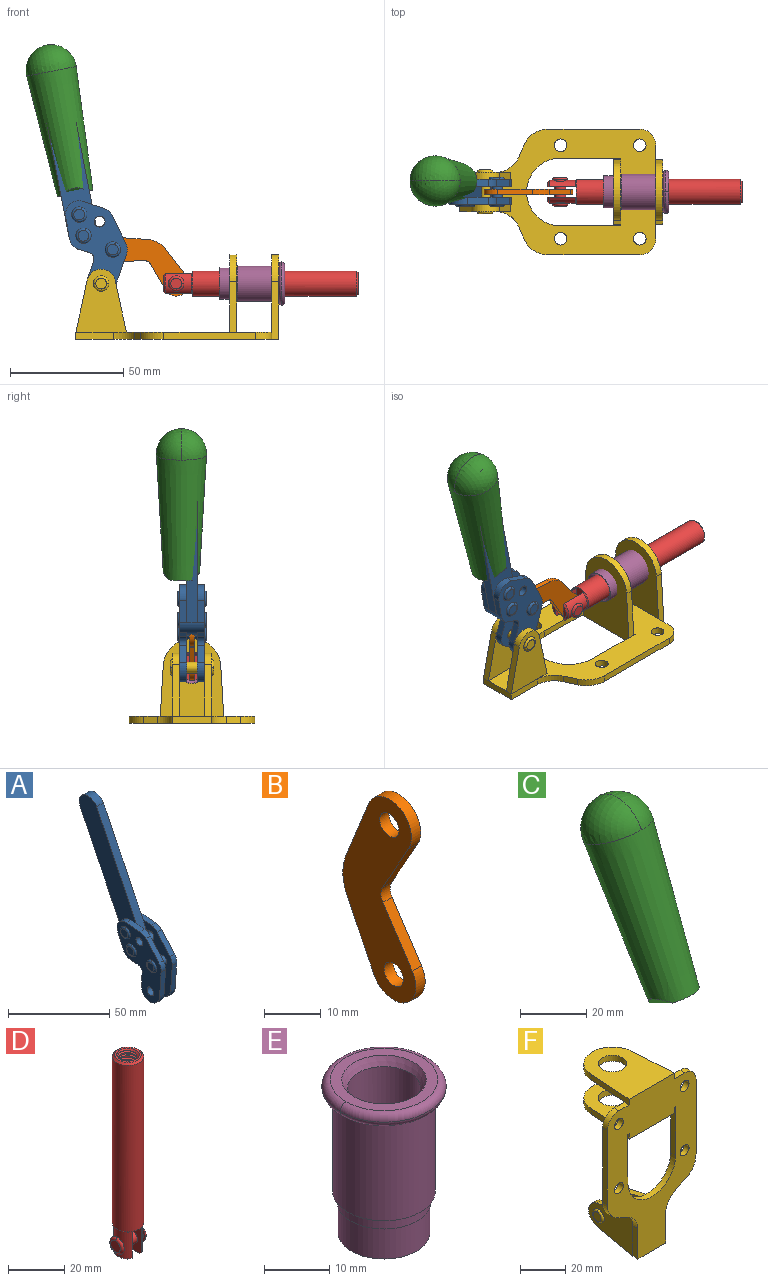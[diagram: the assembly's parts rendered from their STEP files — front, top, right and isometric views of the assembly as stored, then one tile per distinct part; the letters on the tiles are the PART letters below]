
ASSEMBLY  parts=6 mates=6
PART A: 59 faces, bbox 12.9x60.2x99.6 mm
  f0: torus R=2.39mm, axis (-1,0,0), area 14.9mm2, adj f20,f43,f51
  f1: torus R=2.39mm, axis (-1,0,0), area 14.9mm2, adj f19,f42,f51
  f2: torus R=2.39mm, axis (-1,0,0), area 14.9mm2, adj f18,f35,f51
  f3: torus R=2.39mm, axis (-1,0,0), area 14.9mm2, adj f14,f17,f23
  f4: torus R=2.39mm, axis (-1,0,0), area 14.9mm2, adj f13,f16,f23
  f5: torus R=2.39mm, axis (-1,0,0), area 14.9mm2, adj f12,f15,f23
  f6: cylinder r=2.39mm len=4.78mm, axis (1,0,0), area 46.5mm2, adj f48,f50,f51
  f7: cylinder r=2.39mm len=4.78mm, axis (1,0,0), area 46.5mm2, adj f50,f51
  f8: cylinder r=6.35mm len=12.68mm, axis (1,0,0), area 61.8mm2, adj f38,f39,f50,f51
  f9: cylinder r=2.39mm len=4.78mm, axis (-1,0,0), area 70.5mm2, adj f46,f50
  f10: cylinder r=2.39mm len=4.78mm, axis (-1,0,0), area 46.5mm2, adj f23,f45,f46
  f11: cylinder r=2.39mm len=4.78mm, axis (-1,0,0), area 46.5mm2, adj f23,f46
  f12: plane 4.78x4.78mm, normal (1,0,0), area 17.9mm2, adj f5,f15
  f13: plane 4.78x4.78mm, normal (1,0,0), area 17.9mm2, adj f4,f16
  f14: plane 4.78x4.78mm, normal (1,0,0), area 17.9mm2, adj f3,f17
  f15: torus R=2.39mm, axis (-1,0,0), area 14.9mm2, adj f5,f12,f23
  f16: torus R=2.39mm, axis (-1,0,0), area 14.9mm2, adj f4,f13,f23
  f17: torus R=2.39mm, axis (-1,0,0), area 14.9mm2, adj f3,f14,f23
  f18: plane 4.78x4.78mm, normal (-1,0,0), area 17.9mm2, adj f2,f35
  f19: plane 4.78x4.78mm, normal (-1,0,0), area 17.9mm2, adj f1,f42
  f20: plane 4.78x4.78mm, normal (-1,0,0), area 17.9mm2, adj f0,f43
  f21: plane 2.26x0.2mm, normal (1,0,0), area 0.2mm2, adj f31,f44
  f22: plane 2.26x0.2mm, normal (-1,0,0), area 0.2mm2, adj f41,f44
  f23: plane 39.37x30.77mm, normal (1,0,0), area 565.5mm2, adj f3,f4,f5,f10,f11,f15,f16,f17
  f24: cylinder r=6.1mm len=4.15mm, axis (-1,0,0), area 14.7mm2, adj f23,f25,f32,f46
  f25: plane 10.25x9.01mm, normal (0,-0.75,0.66), area 42.3mm2, adj f23,f24,f26,f46
  f26: cylinder r=6.35mm len=4.64mm, axis (-1,0,0), area 15.6mm2, adj f23,f25,f27,f46
  f27: plane 15.84x3.1mm, normal (0,-1,-0.07), area 49.2mm2, adj f23,f26,f28,f46
  f28: cylinder r=6.35mm len=12.68mm, axis (-1,0,0), area 61.8mm2, adj f23,f27,f29,f46
  f29: plane 8.11x3.1mm, normal (0,1,0.07), area 25.2mm2, adj f23,f28,f30,f46
  f30: cylinder r=3.05mm len=3.25mm, axis (-1,0,0), area 14.8mm2, adj f23,f29,f31,f46
  f31: plane 5.99x3.1mm, normal (0,0.07,-1), area 18.6mm2, adj f21,f23,f30,f44,f46
  f32: plane 9.5x3.1mm, normal (0,-0.07,1), area 29.5mm2, adj f23,f24,f33,f46,f47
  f33: cylinder r=6.1mm len=8.63mm, axis (-1,0,0), area 39.1mm2, adj f23,f32,f34,f47
  f34: plane 8.65x3.96mm, normal (0,0.91,-0.42), area 29.5mm2, adj f23,f33,f44,f47
  f35: torus R=2.39mm, axis (-1,0,0), area 14.9mm2, adj f2,f18,f51
  f36: plane 10.25x9.01mm, normal (0,-0.75,0.66), area 42.3mm2, adj f37,f49,f50,f51
  f37: cylinder r=6.35mm len=4.64mm, axis (1,0,0), area 15.6mm2, adj f36,f38,f50,f51
  f38: plane 15.84x3.1mm, normal (0,-1,-0.07), area 49.2mm2, adj f8,f37,f50,f51
  f39: plane 8.11x3.1mm, normal (0,1,0.07), area 25.2mm2, adj f8,f40,f50,f51
  f40: cylinder r=3.05mm len=3.25mm, axis (1,0,0), area 14.8mm2, adj f39,f41,f50,f51
  f41: plane 5.99x3.1mm, normal (0,0.07,-1), area 18.6mm2, adj f22,f40,f44,f50,f51
  f42: torus R=2.39mm, axis (-1,0,0), area 14.9mm2, adj f1,f19,f51
  f43: torus R=2.39mm, axis (-1,0,0), area 14.9mm2, adj f0,f20,f51
  f44: cylinder r=6.35mm len=12.12mm, axis (-1,0,0), area 128.9mm2, adj f21,f22,f23,f31,f34,f41,f46,f47
  f45: plane 2.65x1.35mm, normal (1,0,0), area 1mm2, adj f10,f55
  f46: plane 39.08x20.42mm, normal (-1,0,0), area 412.5mm2, adj f9,f10,f11,f24,f25,f26,f27,f28
  f47: plane 77.62x39.82mm, normal (1,0,0), area 850mm2, adj f32,f33,f34,f44,f53,f54,f55
  f48: plane 2.65x1.35mm, normal (-1,0,0), area 1mm2, adj f6,f55
  f49: cylinder r=6.1mm len=4.15mm, axis (1,0,0), area 14.7mm2, adj f36,f50,f51,f56
  f50: plane 39.08x20.42mm, normal (1,0,0), area 412.5mm2, adj f6,f7,f8,f9,f36,f37,f38,f39
  f51: plane 39.37x30.77mm, normal (-1,0,0), area 565.5mm2, adj f0,f1,f2,f6,f7,f8,f35,f36
  f52: plane 8.65x3.96mm, normal (0,0.91,-0.42), area 29.5mm2, adj f44,f51,f57,f58
  f53: plane 68.49x33.4mm, normal (0,0.9,-0.44), area 358.1mm2, adj f44,f47,f54,f58
  f54: cylinder r=6.35mm len=12.06mm, axis (1,0,0), area 93.7mm2, adj f47,f53,f55,f58
  f55: plane 68.49x33.4mm, normal (0,-0.9,0.44), area 358.1mm2, adj f44,f45,f46,f47,f48,f50,f54,f58
  f56: plane 9.5x3.1mm, normal (0,-0.07,1), area 29.5mm2, adj f49,f50,f51,f57,f58
  f57: cylinder r=6.1mm len=8.63mm, axis (1,0,0), area 39.1mm2, adj f51,f52,f56,f58
  f58: plane 77.62x39.82mm, normal (-1,0,0), area 850mm2, adj f44,f52,f53,f54,f55,f56,f57
PART B: 12 faces, bbox 2.3x18.2x42.8 mm
  f0: cylinder r=2.4mm len=4.8mm, axis (1,0,0), area 34.9mm2, adj f4,f11
  f1: cylinder r=10.41mm len=8.47mm, axis (1,0,0), area 20.2mm2, adj f4,f9,f10,f11
  f2: cylinder r=3.05mm len=3.16mm, axis (1,0,0), area 7.7mm2, adj f4,f6,f7,f11
  f3: cylinder r=2.4mm len=4.8mm, axis (1,0,0), area 34.9mm2, adj f4,f11
  f4: plane 42.81x18.23mm, normal (-1,0,0), area 414.1mm2, adj f0,f1,f2,f3,f5,f6,f7,f8
  f5: cylinder r=5.54mm len=10.67mm, axis (1,0,0), area 41.8mm2, adj f4,f6,f10,f11
  f6: plane 11.66x6.53mm, normal (0,-0.87,-0.49), area 30.9mm2, adj f2,f4,f5,f11
  f7: plane 11.17x7.33mm, normal (0,-0.84,0.55), area 30.9mm2, adj f2,f4,f8,f11
  f8: cylinder r=5.54mm len=10.51mm, axis (1,0,0), area 41.8mm2, adj f4,f7,f9,f11
  f9: plane 13.67x6.67mm, normal (0,0.9,-0.44), area 35.1mm2, adj f1,f4,f8,f11
  f10: plane 14.1x5.7mm, normal (0,0.93,0.37), area 35.1mm2, adj f1,f4,f5,f11
  f11: plane 42.81x18.23mm, normal (1,0,0), area 414.1mm2, adj f0,f1,f2,f3,f5,f6,f7,f8
PART C: 11 faces, bbox 22.3x42.6x64.5 mm
  f0: sphere r=11.13mm, area 411.4mm2, adj f1,f8
  f1: cone r=11.11mm half-angle=3.3deg, axis (0,0.44,0.9), area 3251.8mm2, adj f0,f7,f8,f9,f10
  f2: cylinder r=6.16mm len=11.7mm, axis (1,0,0), area 89.5mm2, adj f3,f4,f5,f6
  f3: plane 60.23x36.75mm, normal (-1,0,0), area 763.6mm2, adj f2,f4,f6,f10
  f4: plane 51.37x25.05mm, normal (0,0.9,-0.44), area 264.2mm2, adj f2,f3,f5,f10
  f5: plane 60.23x36.75mm, normal (1,0,0), area 763.6mm2, adj f2,f4,f6,f10
  f6: plane 51.37x25.05mm, normal (0,-0.9,0.44), area 264.2mm2, adj f2,f3,f5,f10
  f7: plane 9.95x5.95mm, normal (0.71,-0.31,-0.64), area 25.8mm2, adj f1,f10
  f8: sphere r=11.13mm, area 411.4mm2, adj f0,f1
  f9: plane 9.95x5.95mm, normal (-0.71,-0.31,-0.64), area 25.8mm2, adj f1,f10
  f10: plane 14.27x11.38mm, normal (0,-0.44,-0.9), area 106.7mm2, adj f1,f3,f4,f5,f6,f7,f9
PART D: 48 faces, bbox 12.6x11.1x86.1 mm
  f0: torus R=2.41mm, axis (-1,0,0), area 15mm2, adj f30,f32,f34
  f1: torus R=2.41mm, axis (-1,0,0), area 15mm2, adj f29,f31,f33
  f2: cylinder r=5.54mm len=72.39mm, axis (0,0,1), area 2518.5mm2, adj f3,f4,f42,f43
  f3: cone r=5.54mm half-angle=45deg, axis (0,0,1), area 7.6mm2, adj f2,f5,f41
  f4: cone r=5.54mm half-angle=45deg, axis (0,0,-1), area 34.9mm2, adj f2,f39
  f5: cylinder r=5.08mm len=11.48mm, axis (0,0,1), area 108.3mm2, adj f3,f7,f8,f41
  f6: cylinder r=2.41mm len=4.83mm, axis (-1,0,0), area 71.2mm2, adj f40,f41
  f7: cylinder r=2.41mm len=4.83mm, axis (-1,0,0), area 7.6mm2, adj f5,f34
  f8: cone r=5.08mm half-angle=45deg, axis (0,0,1), area 10.6mm2, adj f5,f37,f41
  f9: cone r=3.98mm half-angle=45deg, axis (0,0,1), area 17.6mm2, adj f27,f39,f45,f46,f47
  f10: cylinder r=2.41mm len=4.83mm, axis (-1,0,0), area 7.6mm2, adj f33,f38
  f11: cylinder r=3.2mm len=6.4mm, axis (0,0,1), area 78.4mm2, adj f12,f28,f44,f45,f47
  f12: cylinder r=3.2mm len=6.4mm, axis (0,0,1), area 10.5mm2, adj f11,f13,f45,f47
  f13: cylinder r=3.2mm len=6.4mm, axis (0,0,1), area 10.5mm2, adj f12,f14,f45,f47
  f14: cylinder r=3.2mm len=6.4mm, axis (0,0,1), area 10.5mm2, adj f13,f15,f45,f47
  f15: cylinder r=3.2mm len=6.4mm, axis (0,0,1), area 10.5mm2, adj f14,f16,f45,f47
  f16: cylinder r=3.2mm len=6.4mm, axis (0,0,1), area 10.5mm2, adj f15,f17,f45,f47
  f17: cylinder r=3.2mm len=6.4mm, axis (0,0,1), area 10.5mm2, adj f16,f18,f45,f47
  f18: cylinder r=3.2mm len=6.4mm, axis (0,0,1), area 10.5mm2, adj f17,f19,f45,f47
  f19: cylinder r=3.2mm len=6.4mm, axis (0,0,1), area 10.5mm2, adj f18,f20,f45,f47
  f20: cylinder r=3.2mm len=6.4mm, axis (0,0,1), area 10.5mm2, adj f19,f21,f45,f47
  f21: cylinder r=3.2mm len=6.4mm, axis (0,0,1), area 10.5mm2, adj f20,f22,f45,f47
  f22: cylinder r=3.2mm len=6.4mm, axis (0,0,1), area 10.5mm2, adj f21,f23,f45,f47
  f23: cylinder r=3.2mm len=6.4mm, axis (0,0,1), area 10.5mm2, adj f22,f24,f45,f47
  f24: cylinder r=3.2mm len=6.4mm, axis (0,0,1), area 10.5mm2, adj f23,f25,f45,f47
  f25: cylinder r=3.2mm len=6.4mm, axis (0,0,1), area 10.5mm2, adj f24,f26,f45,f47
  f26: cylinder r=3.2mm len=6.4mm, axis (0,0,1), area 10.5mm2, adj f25,f27,f45,f47
  f27: cylinder r=3.2mm len=6.4mm, axis (0,0,1), area 7.4mm2, adj f9,f26,f45,f47
  f28: cone r=3.2mm half-angle=60deg, axis (0,0,1), area 37.2mm2, adj f11
  f29: plane 4.83x4.83mm, normal (-1,0,0), area 18.3mm2, adj f1,f31
  f30: plane 4.83x4.83mm, normal (1,0,0), area 18.3mm2, adj f0,f32
  f31: torus R=2.41mm, axis (-1,0,0), area 15mm2, adj f1,f29,f33
  f32: torus R=2.41mm, axis (-1,0,0), area 15mm2, adj f0,f30,f34
  f33: plane 6.83x6.83mm, normal (1,0,0), area 18.3mm2, adj f1,f10,f31
  f34: plane 6.83x6.83mm, normal (-1,0,0), area 18.3mm2, adj f0,f7,f32
  f35: cone r=5.08mm half-angle=45deg, axis (0,0,1), area 10.6mm2, adj f36,f38,f40
  f36: plane 7.25x1.97mm, normal (0,0,-1), area 10mm2, adj f35,f40
  f37: plane 7.25x1.97mm, normal (0,0,-1), area 10mm2, adj f8,f41
  f38: cylinder r=5.08mm len=11.48mm, axis (0,0,1), area 108.3mm2, adj f10,f35,f40,f42
  f39: plane 9.55x9.55mm, normal (0,0,1), area 22mm2, adj f4,f9
  f40: plane 12.76x10.09mm, normal (1,0,0), area 95.7mm2, adj f6,f35,f36,f38,f42,f43
  f41: plane 12.76x10.09mm, normal (-1,0,0), area 95.7mm2, adj f3,f5,f6,f8,f37,f43
  f42: cone r=5.54mm half-angle=45deg, axis (0,0,1), area 7.6mm2, adj f2,f38,f40
  f43: plane 11.07x4.7mm, normal (0,0,-1), area 50.4mm2, adj f2,f40,f41
  f44: plane 0.89x0.62mm, normal (-1,0,0), area 0.3mm2, adj f11,f45,f46,f47
  f45: bspline ~24.8x7.63mm, area 266.6mm2, adj f9,f11,f12,f13,f14,f15,f16,f17
  f46: bspline ~24.87x7.63mm, area 73.6mm2, adj f9,f44,f45,f47
  f47: bspline ~24.98x7.63mm, area 272.5mm2, adj f9,f11,f12,f13,f14,f15,f16,f17
PART E: 15 faces, bbox 20.6x20.6x28.7 mm
  f0: torus R=8.26mm, axis (0,0,1), area 56.8mm2, adj f1,f10,f12
  f1: torus R=8.26mm, axis (0,0,1), area 56.8mm2, adj f0,f6,f13
  f2: cylinder r=5.59mm len=25.91mm, axis (0,0,1), area 909.6mm2, adj f3,f4
  f3: cone r=6.86mm half-angle=45deg, axis (0,0,-1), area 70.2mm2, adj f2,f14
  f4: cone r=6.47mm half-angle=30deg, axis (0,0,1), area 66.7mm2, adj f2,f13
  f5: cylinder r=7.04mm len=14.07mm, axis (0,0,1), area 252.6mm2, adj f11,f14
  f6: torus R=8.26mm, axis (0,0,1), area 56.8mm2, adj f1,f12,f13
  f7: cylinder r=7.16mm len=14.33mm, axis (0,0,1), area 91.5mm2, adj f9,f11
  f8: cylinder r=7.86mm len=18.42mm, axis (0,0,1), area 909.6mm2, adj f9,f10
  f9: plane 15.72x15.72mm, normal (0,0,-1), area 33mm2, adj f7,f8
  f10: plane 16.51x16.51mm, normal (0,0,-1), area 19.9mm2, adj f0,f8,f12
  f11: plane 14.33x14.33mm, normal (0,0,-1), area 5.7mm2, adj f5,f7
  f12: torus R=8.26mm, axis (0,0,1), area 56.8mm2, adj f0,f6,f10
  f13: plane 16.51x16.51mm, normal (0,0,1), area 82.7mm2, adj f1,f4,f6
  f14: plane 14.07x14.07mm, normal (0,0,-1), area 7.8mm2, adj f3,f5
PART F: 55 faces, bbox 55.7x37.4x89.8 mm
  f0: torus R=2.41mm, axis (-1,0,0), area 15mm2, adj f11,f15,f25
  f1: torus R=2.41mm, axis (-1,0,0), area 15mm2, adj f10,f12,f22
  f2: cylinder r=2.78mm len=5.56mm, axis (0,-1,0), area 54.2mm2, adj f30,f54
  f3: cylinder r=14.99mm len=29.97mm, axis (0,-1,0), area 145.9mm2, adj f30,f49,f53,f54
  f4: cylinder r=2.78mm len=5.56mm, axis (0,-1,0), area 54.2mm2, adj f30,f54
  f5: cylinder r=2.78mm len=5.56mm, axis (0,-1,0), area 54.2mm2, adj f30,f54
  f6: cylinder r=2.78mm len=5.56mm, axis (0,-1,0), area 54.2mm2, adj f30,f54
  f7: cylinder r=6.35mm len=12.7mm, axis (0,0,1), area 123.6mm2, adj f27,f51
  f8: cylinder r=6.35mm len=12.7mm, axis (0,0,-1), area 124.7mm2, adj f21,f35
  f9: cylinder r=2.41mm len=11.18mm, axis (-1,0,0), area 169.4mm2, adj f16,f19
  f10: plane 4.83x4.83mm, normal (1,0,0), area 18.3mm2, adj f1,f12
  f11: plane 4.83x4.83mm, normal (-1,0,0), area 18.3mm2, adj f0,f15
  f12: torus R=2.41mm, axis (-1,0,0), area 15mm2, adj f1,f10,f22
  f13: cylinder r=6.35mm len=12.41mm, axis (1,0,0), area 53.4mm2, adj f18,f19,f22,f23
  f14: cylinder r=6.35mm len=12.41mm, axis (-1,0,0), area 53.4mm2, adj f16,f17,f24,f25
  f15: torus R=2.41mm, axis (-1,0,0), area 15mm2, adj f0,f11,f25
  f16: plane 27.86x22.35mm, normal (1,0,0), area 425.4mm2, adj f9,f14,f17,f24,f30
  f17: plane 22.86x4.97mm, normal (0,0.21,0.98), area 72.5mm2, adj f14,f16,f25,f30
  f18: plane 22.86x4.97mm, normal (0,0.21,0.98), area 72.5mm2, adj f13,f19,f22,f30
  f19: plane 27.86x22.35mm, normal (-1,0,0), area 425.4mm2, adj f9,f13,f18,f23,f30
  f20: cylinder r=12.7mm len=25.35mm, axis (0,0,-1), area 119.8mm2, adj f21,f34,f35,f36
  f21: plane 34.21x28.07mm, normal (0,0,-1), area 702.4mm2, adj f8,f20,f30,f34,f36
  f22: plane 27.96x22.45mm, normal (1,0,0), area 407.2mm2, adj f1,f12,f13,f18,f23,f30,f42,f43
  f23: plane 22.86x4.97mm, normal (0,0.21,-0.98), area 72.5mm2, adj f13,f19,f22,f44
  f24: plane 22.86x4.97mm, normal (0,0.21,-0.98), area 72.5mm2, adj f14,f16,f25,f44
  f25: plane 27.86x22.35mm, normal (-1,0,0), area 407.1mm2, adj f0,f14,f15,f17,f24,f30,f45,f46
  f26: plane 3.1x0.95mm, normal (0,0,-1), area 2.7mm2, adj f30,f49,f50,f54
  f27: plane 34.21x28.07mm, normal (0,0,1), area 702.4mm2, adj f7,f28,f30,f50,f52
  f28: cylinder r=12.7mm len=25.35mm, axis (0,0,1), area 118.8mm2, adj f27,f50,f51,f52
  f29: plane 3.1x0.95mm, normal (0,0,-1), area 2.7mm2, adj f30,f52,f53,f54
  f30: plane 86.54x55.63mm, normal (0,1,0), area 2362.9mm2, adj f2,f3,f4,f5,f6,f16,f17,f18
  f31: plane 40.56x3.1mm, normal (-1,0,0), area 125.7mm2, adj f30,f32,f48,f54
  f32: cylinder r=7.11mm len=7.11mm, axis (0,-1,0), area 34.6mm2, adj f30,f31,f33,f54
  f33: plane 6.67x3.1mm, normal (0,0,1), area 20.4mm2, adj f30,f32,f34,f54
  f34: plane 25.39x3.13mm, normal (-1,0.06,0), area 79.5mm2, adj f20,f21,f33,f35,f54
  f35: plane 37.31x28.45mm, normal (0,0,1), area 789.9mm2, adj f8,f20,f34,f36,f54
  f36: plane 25.39x3.13mm, normal (1,0.06,0), area 79.5mm2, adj f20,f21,f35,f37,f54
  f37: plane 6.67x3.1mm, normal (0,0,1), area 20.4mm2, adj f30,f36,f38,f54
  f38: cylinder r=7.11mm len=7.11mm, axis (0,-1,0), area 34.6mm2, adj f30,f37,f39,f54
  f39: plane 40.56x3.1mm, normal (1,0,0), area 125.7mm2, adj f30,f38,f40,f54
  f40: cylinder r=11.18mm len=10.16mm, axis (0,-1,0), area 39.5mm2, adj f30,f39,f41,f54
  f41: plane 6.09x3.1mm, normal (0.42,0,-0.91), area 20.8mm2, adj f30,f40,f42,f54
  f42: cylinder r=11.18mm len=9.41mm, axis (0,-1,0), area 37.2mm2, adj f22,f30,f41,f43,f54
  f43: plane 16.5x3.1mm, normal (1,0,0), area 51.1mm2, adj f22,f42,f44,f54
  f44: plane 17.37x3.1mm, normal (0,0,-1), area 53.8mm2, adj f23,f24,f30,f43,f45,f54
  f45: plane 16.5x3.1mm, normal (-1,0,0), area 51.1mm2, adj f25,f44,f46,f54
  f46: cylinder r=11.18mm len=9.41mm, axis (0,-1,0), area 37.2mm2, adj f25,f30,f45,f47,f54
  f47: plane 6.09x3.1mm, normal (-0.42,0,-0.91), area 20.8mm2, adj f30,f46,f48,f54
  f48: cylinder r=11.18mm len=10.16mm, axis (0,-1,0), area 39.5mm2, adj f30,f31,f47,f54
  f49: plane 26.54x3.1mm, normal (-1,0,0), area 82.3mm2, adj f3,f26,f30,f54
  f50: plane 25.39x3.1mm, normal (1,0.06,0), area 78.8mm2, adj f26,f27,f28,f51,f54
  f51: plane 37.31x28.45mm, normal (0,0,-1), area 789.9mm2, adj f7,f28,f50,f52,f54
  f52: plane 25.39x3.1mm, normal (-1,0.06,0), area 78.8mm2, adj f27,f28,f29,f51,f54
  f53: plane 26.54x3.1mm, normal (1,0,0), area 82.3mm2, adj f3,f29,f30,f54
  f54: plane 89.66x55.63mm, normal (0,-1,0), area 2678.5mm2, adj f2,f3,f4,f5,f6,f26,f29,f31
PLACE A rot(axis=(0.13,0.13,0.98),91deg) t=(-31.57,1.41,49.39)mm
PLACE B rot(axis=(0.66,0.66,0.38),138.7deg) t=(-56.27,1.41,11.27)mm
PLACE C rot(axis=(0.13,0.13,0.98),91deg) t=(-31.57,6.07,49.39)mm
PLACE D rot(axis=(-0.58,0.58,-0.58),120deg) t=(-45.98,1.41,49.37)mm
PLACE E rot(axis=(0,1,0),90deg) t=(-31.56,-23.2,24.76)mm
PLACE F rot(axis=(0.58,0.58,0.58),120deg) t=(-31.56,1.41,0.14)mm fixed
MATE slider D.f2 <-> F.f7  axis (1,0,0) through (12.8,1.41,24.76)mm
MATE revolute B.f3 <-> A.f4  axis (0,1,0) through (-58.49,1.41,39.77)mm
MATE revolute A.f7 <-> F.f0  axis (0,-1,0) through (-63.65,1.41,24.76)mm
MATE fastened E.f2 <-> F.f7  axis (-1,0,0) through (14.83,1.41,24.76)mm
MATE revolute B.f5 <-> D.f6  axis (0,1,0) through (-30.51,1.41,24.76)mm
MATE fastened C.f2 <-> A.f54  axis (0,1,0) through (-86.02,3.76,120.68)mm
